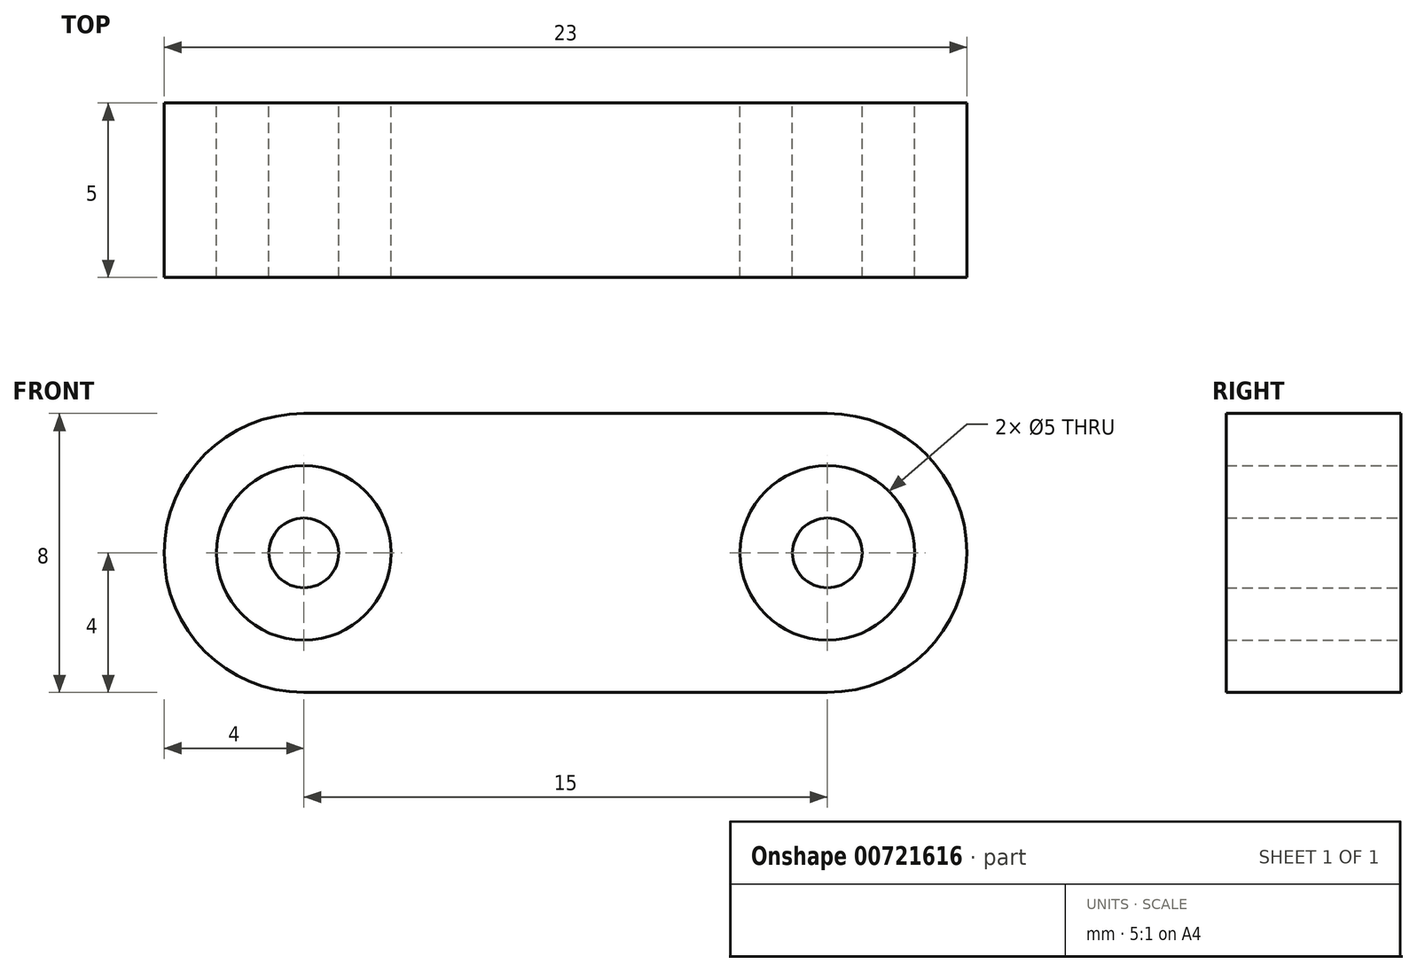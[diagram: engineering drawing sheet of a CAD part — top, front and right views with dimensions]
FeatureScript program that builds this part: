
annotation { "Feature Type Name" : "Feature", "Feature Type Description" : "" }
export const myFeature = defineFeature(function(context is Context, id is Id, definition is map)
    precondition{}
    {
        {
            var Q0;
            Q0=qCreatedBy(makeId("Front.planeOp"),FACE);
            var sketch = newSketch(context, id + "F0", { "sketchPlane" : qUnion([Q0])});
            skLineSegment(sketch, "E0.bottom", {"start": v(7.5, 4) * mm, "end": v(-7.5, 4) * mm});
            skLineSegment(sketch, "E0.top", {"start": v(7.5, -4) * mm, "end": v(-7.5, -4) * mm});
            skPoint(sketch, "E0.middle", {"position": v(0, 0) * mm});
            skArc(sketch, "E1", {"start": v(-7.5, 4) * mm, "mid": v(-11.5, 0) * mm, "end": v(-7.5, -4) * mm});
            skArc(sketch, "E2", {"start": v(7.5, -4) * mm, "mid": v(11.5, 0) * mm, "end": v(7.5, 4) * mm});
            skCircle(sketch, "E3", {"center": v(-7.5, 0) * mm, "radius": 2.5 * mm});
            skCircle(sketch, "E4", {"center": v(-7.5, 0) * mm, "radius": 1 * mm});
            skCircle(sketch, "E5", {"center": v(7.5, 0) * mm, "radius": 1 * mm});
            skCircle(sketch, "E6", {"center": v(7.5, 0) * mm, "radius": 2.5 * mm});
            skSolve(sketch);
        }
        {
            var Q0;
            Q0=makeQuery(id+"F0.imprint","IMPRINT",FACE,{"disambiguationData":[TD([[makeQuery(id+"F0.imprint","IMPRINT",EDGE,{"derivedFrom":sQuery(id+"F0.wireOp",EDGE,"E0.bottom")}),1.0]])]});
            var Q1;
            Q1=makeQuery(id+"F0.imprint","IMPRINT",FACE,{"disambiguationData":[TD([[makeQuery(id+"F0.imprint","IMPRINT",EDGE,{"derivedFrom":sQuery(id+"F0.wireOp",EDGE,"E4")}),1.0]])]});
            var Q2;
            Q2=makeQuery(id+"F0.imprint","IMPRINT",FACE,{"disambiguationData":[TD([[makeQuery(id+"F0.imprint","IMPRINT",EDGE,{"derivedFrom":sQuery(id+"F0.wireOp",EDGE,"E5")}),1.0]])]});
            extrude(context, id + "F1", {"entities" : qUnion([Q0, Q1, Q2]), "endBound" : BoundingType.SYMMETRIC, "depth" : 5 * mm, "offsetDistance" : 25.4 * mm});
        }
    });
